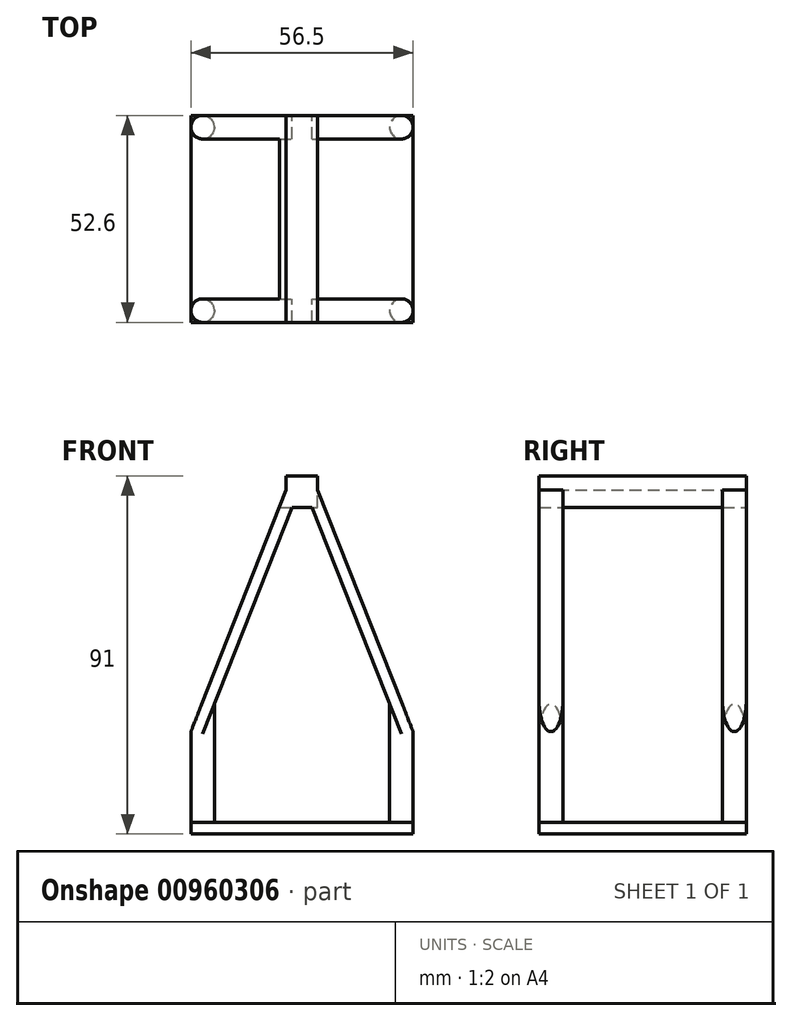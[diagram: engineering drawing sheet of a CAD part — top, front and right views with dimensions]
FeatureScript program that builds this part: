
annotation { "Feature Type Name" : "Feature", "Feature Type Description" : "" }
export const myFeature = defineFeature(function(context is Context, id is Id, definition is map)
    precondition{}
    {
        {
            var Q0;
            Q0=qCreatedBy(makeId("Front.planeOp"),FACE);
            var sketch = newSketch(context, id + "F0", { "sketchPlane" : qUnion([Q0])});
            skLineSegment(sketch, "E0", {"start": v(-28.25, 0) * mm, "end": v(-28.25, 22.98) * mm});
            skLineSegment(sketch, "E1.0", {"start": v(-22.25, 0) * mm, "end": v(-22.25, 30) * mm});
            skLineSegment(sketch, "E2", {"start": v(-25.25, 33.55) * mm, "end": v(-25.25, 26.27) * mm, "construction": true});
            skLineSegment(sketch, "E3", {"start": v(-28.25, 0) * mm, "end": v(-28.25, -3) * mm});
            skLineSegment(sketch, "E4", {"start": v(-28.25, 0) * mm, "end": v(-22.25, 0) * mm});
            skLineSegment(sketch, "E5", {"start": v(0, 87.78) * mm, "end": v(0, -3) * mm, "construction": true});
            skLineSegment(sketch, "E6", {"start": v(-2.5, 80) * mm, "end": v(0, 80) * mm});
            skLineSegment(sketch, "E7", {"start": v(-4, 84.37) * mm, "end": v(-4, 88) * mm});
            skLineSegment(sketch, "E8", {"start": v(-4, 88) * mm, "end": v(0, 88) * mm});
            skLineSegment(sketch, "E9", {"start": v(0, 88) * mm, "end": v(0, 87.78) * mm});
            skLineSegment(sketch, "E10", {"start": v(-22.25, 0) * mm, "end": v(0, 0) * mm});
            skLineSegment(sketch, "E11", {"start": v(0, -3) * mm, "end": v(-28.25, -3) * mm});
            skLineSegment(sketch, "E12", {"start": v(-48.17, 30) * mm, "end": v(25.31, 30) * mm, "construction": true});
            skLineSegment(sketch, "E13", {"start": v(-2.5, 80) * mm, "end": v(-22.25, 30) * mm});
            skLineSegment(sketch, "E14.0", {"start": v(-4, 84.37) * mm, "end": v(-28.25, 22.98) * mm});
            skPoint(sketch, "E15.orphan", {"position": v(-4, 80) * mm});
            skLineSegment(sketch, "E16", {"start": v(-22.25, 30) * mm, "end": v(-28.25, 22.98) * mm});
            skLineSegment(sketch, "E17", {"start": v(0, 80) * mm, "end": v(0, 87.78) * mm, "construction": true});
            skLineSegment(sketch, "E18", {"start": v(0, 87.78) * mm, "end": v(0, 80) * mm});
            skLineSegment(sketch, "E19", {"start": v(0, 0) * mm, "end": v(0, -3) * mm});
            skLineSegment(sketch, "E20.MirrorCS", {"start": v(4, 88) * mm, "end": v(0, 88) * mm});
            skLineSegment(sketch, "E21.MirrorCS", {"start": v(4, 84.37) * mm, "end": v(4, 88) * mm});
            skLineSegment(sketch, "E22.MirrorCS", {"start": v(4, 84.37) * mm, "end": v(28.25, 22.98) * mm});
            skLineSegment(sketch, "E23.MirrorCS", {"start": v(2.5, 80) * mm, "end": v(0, 80) * mm});
            skLineSegment(sketch, "E24.MirrorCS", {"start": v(2.5, 80) * mm, "end": v(22.25, 30) * mm});
            skLineSegment(sketch, "E25.MirrorCS", {"start": v(22.25, 30) * mm, "end": v(28.25, 22.98) * mm});
            skLineSegment(sketch, "E26.MirrorCS", {"start": v(22.25, 0) * mm, "end": v(22.25, 30) * mm});
            skLineSegment(sketch, "E27.MirrorCS", {"start": v(28.25, 0) * mm, "end": v(28.25, 22.98) * mm});
            skLineSegment(sketch, "E28.MirrorCS", {"start": v(28.25, 0) * mm, "end": v(22.25, 0) * mm});
            skLineSegment(sketch, "E29.MirrorCS", {"start": v(22.25, 0) * mm, "end": v(0, 0) * mm});
            skLineSegment(sketch, "E30.MirrorCS", {"start": v(0, -3) * mm, "end": v(28.25, -3) * mm});
            skLineSegment(sketch, "E31.MirrorCS", {"start": v(28.25, 0) * mm, "end": v(28.25, -3) * mm});
            skLineSegment(sketch, "E32", {"start": v(-28.25, 22.98) * mm, "end": v(-28.25, 30) * mm});
            skLineSegment(sketch, "E33", {"start": v(-28.25, 30) * mm, "end": v(-25.48, 30) * mm});
            skLineSegment(sketch, "E34", {"start": v(28.25, 22.98) * mm, "end": v(28.25, 30) * mm});
            skLineSegment(sketch, "E35", {"start": v(28.25, 30) * mm, "end": v(25.48, 30) * mm});
            skLineSegment(sketch, "E36", {"start": v(-22.25, 30) * mm, "end": v(-25.25, 22.4) * mm});
            skLineSegment(sketch, "E37", {"start": v(22.25, 30) * mm, "end": v(25.25, 22.4) * mm});
            skLineSegment(sketch, "E38", {"start": v(-25.25, 26.49) * mm, "end": v(-25.25, 22.4) * mm});
            skLineSegment(sketch, "E39", {"start": v(25.25, 22.4) * mm, "end": v(25.25, 26.49) * mm});
            skLineSegment(sketch, "E40", {"start": v(-4, 84.37) * mm, "end": v(-1.2, 83.27) * mm, "construction": true});
            skLineSegment(sketch, "E41", {"start": v(-2.5, 80) * mm, "end": v(-1.2, 83.27) * mm, "construction": true});
            skLineSegment(sketch, "E42", {"start": v(-28.25, 22.98) * mm, "end": v(-25.46, 21.87) * mm, "construction": true});
            skLineSegment(sketch, "E43", {"start": v(-25.25, 22.4) * mm, "end": v(-25.46, 21.87) * mm, "construction": true});
            skLineSegment(sketch, "E44", {"start": v(2.5, 80) * mm, "end": v(4, 80) * mm, "construction": true});
            skLineSegment(sketch, "E45", {"start": v(4, 80) * mm, "end": v(4, 84.37) * mm, "construction": true});
            skSolve(sketch);
        }
        {
            var Q0;
            Q0=makeQuery(id+"F0.imprint","IMPRINT",FACE,{"disambiguationData":[TD([[makeQuery(id+"F0.imprint","IMPRINT",EDGE,{"derivedFrom":sQuery(id+"F0.wireOp",EDGE,"E6")}),1.0]])]});
            var Q1;
            Q1=makeQuery(id+"F0.imprint","IMPRINT",FACE,{"disambiguationData":[TD([[makeQuery(id+"F0.imprint","IMPRINT",EDGE,{"derivedFrom":sQuery(id+"F0.wireOp",EDGE,"E9")}),1.0]])]});
            var Q2;
            Q2=makeQuery(id+"F0.imprint","IMPRINT",FACE,{"disambiguationData":[TD([[makeQuery(id+"F0.imprint","IMPRINT",EDGE,{"derivedFrom":sQuery(id+"F0.wireOp",EDGE,"E3")}),1.0]])]});
            var Q3;
            Q3=makeQuery(id+"F0.imprint","IMPRINT",FACE,{"disambiguationData":[TD([[makeQuery(id+"F0.imprint","IMPRINT",EDGE,{"derivedFrom":sQuery(id+"F0.wireOp",EDGE,"E19")}),1.0]])]});
            var Q4;
            {var subQ0=sQuery(id+"F0.wireOp",EDGE,"E36");Q4=makeQuery(id+"F0.imprint","IMPRINT",FACE,{"disambiguationData":[TD([[makeQuery(id+"F0.imprint","IMPRINT",EDGE,{"derivedFrom":subQ0}),-1.0]])]});}
            var Q5;
            {var subQ0=sQuery(id+"F0.wireOp",EDGE,"E37");Q5=makeQuery(id+"F0.imprint","IMPRINT",FACE,{"disambiguationData":[TD([[makeQuery(id+"F0.imprint","IMPRINT",EDGE,{"derivedFrom":subQ0}),1.0]])]});}
            extrude(context, id + "F1", {"entities" : qUnion([Q0, Q1, Q2, Q3, Q4, Q5]), "endBound" : BoundingType.SYMMETRIC, "depth" : 52.6 * mm, "offsetDistance" : 25 * mm});
        }
        {
            var Q0;
            Q0=qCreatedBy(makeId("Top.planeOp"),FACE);
            var sketch = newSketch(context, id + "F2", { "sketchPlane" : qUnion([Q0])});
            skLineSegment(sketch, "E46.0.0", {"start": v(28.25, 26.3) * mm, "end": v(-28.25, 26.3) * mm});
            skLineSegment(sketch, "E46.0.1", {"start": v(-28.25, 26.3) * mm, "end": v(-28.25, -26.3) * mm});
            skLineSegment(sketch, "E46.0.2", {"start": v(-28.25, -26.3) * mm, "end": v(28.25, -26.3) * mm});
            skLineSegment(sketch, "E46.0.3", {"start": v(28.25, -26.3) * mm, "end": v(28.25, 26.3) * mm});
            skCircle(sketch, "E47", {"center": v(-25.25, 23.3) * mm, "radius": 3 * mm});
            skCircle(sketch, "E48", {"center": v(25.25, 23.3) * mm, "radius": 3 * mm});
            skCircle(sketch, "E49", {"center": v(-25.25, -23.3) * mm, "radius": 3 * mm});
            skCircle(sketch, "E50", {"center": v(25.25, -23.3) * mm, "radius": 3 * mm});
            skSolve(sketch);
        }
        {
            var Q0;
            {var subQ0=sQuery(id+"F2.wireOp",EDGE,"E47");var subQ1=makeQuery(id+"F2.imprint","INTERSECT",VERTEX,{"derivedFrom":[sQuery(id+"F2.wireOp",EDGE,"E46.0.0"),subQ0]});Q0=makeQuery(id+"F2.imprint","IMPRINT",FACE,{"disambiguationData":[TD([[makeQuery(id+"F2.imprint","IMPRINT",EDGE,{"disambiguationData":[TD([[subQ1,-1.0]])],"derivedFrom":subQ0}),1.0]])]});}
            var Q1;
            {var subQ0=sQuery(id+"F2.wireOp",EDGE,"E49");var subQ1=makeQuery(id+"F2.imprint","INTERSECT",VERTEX,{"derivedFrom":[sQuery(id+"F2.wireOp",EDGE,"E46.0.1"),subQ0]});Q1=makeQuery(id+"F2.imprint","IMPRINT",FACE,{"disambiguationData":[TD([[makeQuery(id+"F2.imprint","IMPRINT",EDGE,{"disambiguationData":[TD([[subQ1,-1.0]])],"derivedFrom":subQ0}),1.0]])]});}
            var Q2;
            {var subQ0=sQuery(id+"F2.wireOp",EDGE,"E48");var subQ1=makeQuery(id+"F2.imprint","INTERSECT",VERTEX,{"derivedFrom":[sQuery(id+"F2.wireOp",EDGE,"E46.0.0"),subQ0]});Q2=makeQuery(id+"F2.imprint","IMPRINT",FACE,{"disambiguationData":[TD([[makeQuery(id+"F2.imprint","IMPRINT",EDGE,{"disambiguationData":[TD([[subQ1,1.0]])],"derivedFrom":subQ0}),1.0]])]});}
            var Q3;
            {var subQ0=sQuery(id+"F2.wireOp",EDGE,"E50");var subQ1=makeQuery(id+"F2.imprint","INTERSECT",VERTEX,{"derivedFrom":[sQuery(id+"F2.wireOp",EDGE,"E46.0.2"),subQ0]});Q3=makeQuery(id+"F2.imprint","IMPRINT",FACE,{"disambiguationData":[TD([[makeQuery(id+"F2.imprint","IMPRINT",EDGE,{"disambiguationData":[TD([[subQ1,1.0]])],"derivedFrom":subQ0}),1.0]])]});}
            extrude(context, id + "F3", {"entities" : qUnion([Q0, Q1, Q2, Q3]), "depth" : 30 * mm, "offsetDistance" : 25 * mm});
        }
        {
            var Q0;
            Q0=makeQuery(id+"F3.opExtrude","CAP_FACE",FACE,{"disambiguationData":[OSD([sQuery(id+"F2.wireOp",EDGE,"E48")])],"isStart":false});
            cPlane(context, id + "F4", {"entities" : qUnion([Q0]), "cplaneType" : CPlaneType.OFFSET, "offset" : 0 * mm, "width" : 150 * mm, "height" : 150 * mm});
        }
        {
            var Q0;
            Q0=qCreatedBy(id+"F4.planeOp",FACE);
            var sketch = newSketch(context, id + "F5", { "sketchPlane" : qUnion([Q0])});
            skLineSegment(sketch, "E51.0", {"start": v(28.25, -26.3) * mm, "end": v(28.25, -23.3) * mm});
            skLineSegment(sketch, "E52.0", {"start": v(25.25, 26.3) * mm, "end": v(28.25, 26.3) * mm});
            skLineSegment(sketch, "E53.0", {"start": v(-25.25, 26.3) * mm, "end": v(-28.25, 26.3) * mm});
            skLineSegment(sketch, "E54.0", {"start": v(-28.25, -26.3) * mm, "end": v(-28.25, -23.3) * mm});
            skLineSegment(sketch, "E55.0", {"start": v(-25.25, -26.3) * mm, "end": v(-28.25, -26.3) * mm});
            skLineSegment(sketch, "E56.0", {"start": v(25.25, -26.3) * mm, "end": v(28.25, -26.3) * mm});
            skArc(sketch, "E57.0", {"start": v(28.25, 23.3) * mm, "mid": v(27.37, 25.42) * mm, "end": v(25.25, 26.3) * mm});
            skArc(sketch, "E58.0", {"start": v(25.25, -26.3) * mm, "mid": v(27.37, -25.42) * mm, "end": v(28.25, -23.3) * mm});
            skArc(sketch, "E59.0", {"start": v(-28.25, -23.3) * mm, "mid": v(-27.37, -25.42) * mm, "end": v(-25.25, -26.3) * mm});
            skArc(sketch, "E60.0", {"start": v(-25.25, 26.3) * mm, "mid": v(-27.37, 25.42) * mm, "end": v(-28.25, 23.3) * mm});
            skLineSegment(sketch, "E61.trimOffspring", {"start": v(-28.25, 23.3) * mm, "end": v(-28.25, 26.3) * mm});
            skPoint(sketch, "E62.orphan", {"position": v(-4, 26.3) * mm});
            skPoint(sketch, "E63.orphan", {"position": v(-4, -26.3) * mm});
            skPoint(sketch, "E64.orphan", {"position": v(4, 26.3) * mm});
            skLineSegment(sketch, "E65.trimOffspring", {"start": v(28.25, 23.3) * mm, "end": v(28.25, 26.3) * mm});
            skPoint(sketch, "E66.orphan", {"position": v(4, -26.3) * mm});
            skLineSegment(sketch, "E67.0", {"start": v(-28.25, -26.3) * mm, "end": v(-28.25, -20.3) * mm});
            skLineSegment(sketch, "E68.0", {"start": v(28.25, -26.3) * mm, "end": v(28.25, -20.3) * mm});
            skCircle(sketch, "E69.0", {"center": v(25.25, 23.3) * mm, "radius": 3 * mm});
            skCircle(sketch, "E70.0.0", {"center": v(25.25, -23.3) * mm, "radius": 3 * mm});
            skCircle(sketch, "E71.0.0", {"center": v(-25.25, -23.3) * mm, "radius": 3 * mm});
            skCircle(sketch, "E72.0.0", {"center": v(-25.25, 23.3) * mm, "radius": 3 * mm});
            skLineSegment(sketch, "E73", {"start": v(-25.25, 20.3) * mm, "end": v(-28.25, 20.3) * mm});
            skLineSegment(sketch, "E74", {"start": v(25.25, 20.3) * mm, "end": v(28.25, 20.3) * mm});
            skLineSegment(sketch, "E75", {"start": v(25.25, -20.3) * mm, "end": v(28.25, -20.3) * mm});
            skLineSegment(sketch, "E76", {"start": v(-25.25, -20.3) * mm, "end": v(-28.25, -20.3) * mm});
            skLineSegment(sketch, "E77.trimOffspring", {"start": v(-28.25, 20.3) * mm, "end": v(-28.25, 26.3) * mm});
            skLineSegment(sketch, "E78.trimOffspring", {"start": v(28.25, 20.3) * mm, "end": v(28.25, 26.3) * mm});
            skSolve(sketch);
        }
        {
            var Q0;
            Q0=makeQuery(id+"F1.opExtrude","SWEPT_BODY",BODY,{"disambiguationData":[OSD([sQuery(id+"F0.wireOp",EDGE,"E3"),sQuery(id+"F0.wireOp",EDGE,"E4"),sQuery(id+"F0.wireOp",EDGE,"E10"),sQuery(id+"F0.wireOp",EDGE,"E11"),sQuery(id+"F0.wireOp",EDGE,"E28.MirrorCS"),sQuery(id+"F0.wireOp",EDGE,"E29.MirrorCS"),sQuery(id+"F0.wireOp",EDGE,"E30.MirrorCS"),sQuery(id+"F0.wireOp",EDGE,"E31.MirrorCS")])]});
            var Q1;
            Q1=makeQuery(id+"F3.opExtrude","SWEPT_BODY",BODY,{"disambiguationData":[OSD([sQuery(id+"F2.wireOp",EDGE,"E49")])]});
            var Q2;
            Q2=makeQuery(id+"F3.opExtrude","SWEPT_BODY",BODY,{"disambiguationData":[OSD([sQuery(id+"F2.wireOp",EDGE,"E47")])]});
            var Q3;
            Q3=makeQuery(id+"F3.opExtrude","SWEPT_BODY",BODY,{"disambiguationData":[OSD([sQuery(id+"F2.wireOp",EDGE,"E48")])]});
            var Q4;
            Q4=makeQuery(id+"F3.opExtrude","SWEPT_BODY",BODY,{"disambiguationData":[OSD([sQuery(id+"F2.wireOp",EDGE,"E50")])]});
            var Q5;
            Q5=makeQuery(id+"F1.opExtrude","SWEPT_BODY",BODY,{"disambiguationData":[OSD([sQuery(id+"F0.wireOp",EDGE,"E6"),sQuery(id+"F0.wireOp",EDGE,"E7"),sQuery(id+"F0.wireOp",EDGE,"E8"),sQuery(id+"F0.wireOp",EDGE,"E13"),sQuery(id+"F0.wireOp",EDGE,"E14.0"),sQuery(id+"F0.wireOp",EDGE,"E16"),sQuery(id+"F0.wireOp",EDGE,"E20.MirrorCS"),sQuery(id+"F0.wireOp",EDGE,"E21.MirrorCS"),sQuery(id+"F0.wireOp",EDGE,"E22.MirrorCS"),sQuery(id+"F0.wireOp",EDGE,"E23.MirrorCS"),sQuery(id+"F0.wireOp",EDGE,"E24.MirrorCS"),sQuery(id+"F0.wireOp",EDGE,"E25.MirrorCS")])]});
            booleanBodies(context, id + "F6", {"operationType" : BooleanOperationType.UNION, "tools" : qUnion([Q0, Q1, Q2, Q3, Q4, Q5])});
        }
        {
            var Q0;
            {var subQ0=sQuery(id+"F5.wireOp",EDGE,"E53.0");Q0=makeQuery(id+"F5.imprint","IMPRINT",FACE,{"disambiguationData":[TD([[makeQuery(id+"F5.imprint","IMPRINT",EDGE,{"derivedFrom":subQ0}),1.0]])]});}
            var Q1;
            {var subQ0=sQuery(id+"F5.wireOp",EDGE,"E73");Q1=makeQuery(id+"F5.imprint","IMPRINT",FACE,{"disambiguationData":[TD([[makeQuery(id+"F5.imprint","IMPRINT",EDGE,{"derivedFrom":subQ0}),-1.0]])]});}
            var Q2;
            {var subQ0=sQuery(id+"F5.wireOp",EDGE,"E52.0");Q2=makeQuery(id+"F5.imprint","IMPRINT",FACE,{"disambiguationData":[TD([[makeQuery(id+"F5.imprint","IMPRINT",EDGE,{"derivedFrom":subQ0}),-1.0]])]});}
            var Q3;
            {var subQ0=sQuery(id+"F5.wireOp",EDGE,"E74");Q3=makeQuery(id+"F5.imprint","IMPRINT",FACE,{"disambiguationData":[TD([[makeQuery(id+"F5.imprint","IMPRINT",EDGE,{"derivedFrom":subQ0}),1.0]])]});}
            var Q4;
            {var subQ0=sQuery(id+"F5.wireOp",EDGE,"E75");Q4=makeQuery(id+"F5.imprint","IMPRINT",FACE,{"disambiguationData":[TD([[makeQuery(id+"F5.imprint","IMPRINT",EDGE,{"derivedFrom":subQ0}),-1.0]])]});}
            var Q5;
            {var subQ0=sQuery(id+"F5.wireOp",EDGE,"E56.0");Q5=makeQuery(id+"F5.imprint","IMPRINT",FACE,{"disambiguationData":[TD([[makeQuery(id+"F5.imprint","IMPRINT",EDGE,{"derivedFrom":subQ0}),1.0]])]});}
            var Q6;
            {var subQ0=sQuery(id+"F5.wireOp",EDGE,"E76");Q6=makeQuery(id+"F5.imprint","IMPRINT",FACE,{"disambiguationData":[TD([[makeQuery(id+"F5.imprint","IMPRINT",EDGE,{"derivedFrom":subQ0}),1.0]])]});}
            var Q7;
            {var subQ0=sQuery(id+"F5.wireOp",EDGE,"E55.0");Q7=makeQuery(id+"F5.imprint","IMPRINT",FACE,{"disambiguationData":[TD([[makeQuery(id+"F5.imprint","IMPRINT",EDGE,{"derivedFrom":subQ0}),-1.0]])]});}
            extrude(context, id + "F7", {"entities" : qUnion([Q0, Q1, Q2, Q3, Q4, Q5, Q6, Q7]), "operationType" : NewBodyOperationType.REMOVE, "oppositeDirection" : true, "depth" : 8 * mm, "offsetDistance" : 25 * mm});
        }
        {
            var Q0;
            {var subQ0=sQuery(id+"F0.wireOp",EDGE,"E34");Q0=makeQuery(id+"F0.imprint","IMPRINT",FACE,{"disambiguationData":[TD([[makeQuery(id+"F0.imprint","IMPRINT",EDGE,{"derivedFrom":subQ0}),1.0]])]});}
            var Q1;
            {var subQ0=sQuery(id+"F0.wireOp",EDGE,"E32");Q1=makeQuery(id+"F0.imprint","IMPRINT",FACE,{"disambiguationData":[TD([[makeQuery(id+"F0.imprint","IMPRINT",EDGE,{"derivedFrom":subQ0}),-1.0]])]});}
            extrude(context, id + "F8", {"entities" : qUnion([Q0, Q1]), "operationType" : NewBodyOperationType.REMOVE, "endBound" : BoundingType.SYMMETRIC, "oppositeDirection" : true, "depth" : 60 * mm, "offsetDistance" : 25 * mm});
        }
        {
            var Q0;
            Q0=qCreatedBy(makeId("Right.planeOp"),FACE);
            var sketch = newSketch(context, id + "F9", { "sketchPlane" : qUnion([Q0])});
            skLineSegment(sketch, "E79.0", {"start": v(-23.3, 0) * mm, "end": v(23.3, 0) * mm});
            skLineSegment(sketch, "E80", {"start": v(20.3, 0) * mm, "end": v(20.3, 80) * mm});
            skLineSegment(sketch, "E81", {"start": v(-20.3, 0) * mm, "end": v(-20.3, 80) * mm});
            skLineSegment(sketch, "E82", {"start": v(20.3, 80) * mm, "end": v(-20.3, 80) * mm});
            skSolve(sketch);
        }
        {
            var Q0;
            {var subQ0=sQuery(id+"F9.wireOp",EDGE,"E80");Q0=makeQuery(id+"F9.imprint","IMPRINT",FACE,{"disambiguationData":[TD([[makeQuery(id+"F9.imprint","IMPRINT",EDGE,{"derivedFrom":subQ0}),1.0]])]});}
            extrude(context, id + "F10", {"entities" : qUnion([Q0]), "operationType" : NewBodyOperationType.REMOVE, "endBound" : BoundingType.SYMMETRIC, "oppositeDirection" : true, "depth" : 60 * mm, "offsetDistance" : 25 * mm});
        }
        {
            var Q0;
            Q0=makeQuery(id+"F1.opExtrude","SWEPT_FACE",FACE,{"disambiguationData":[OSD([sQuery(id+"F0.wireOp",EDGE,"E8"),sQuery(id+"F0.wireOp",EDGE,"E20.MirrorCS")])]});
            cPlane(context, id + "F11", {"entities" : qUnion([Q0]), "cplaneType" : CPlaneType.OFFSET, "offset" : 0 * mm, "width" : 150 * mm, "height" : 150 * mm});
        }
        {
            var Q0;
            Q0=qCreatedBy(id+"F11.planeOp",FACE);
            var sketch = newSketch(context, id + "F12", { "sketchPlane" : qUnion([Q0])});
            skLineSegment(sketch, "E83.0.1", {"start": v(-4, 20.3) * mm, "end": v(-4, -20.3) * mm});
            skLineSegment(sketch, "E83.0.3", {"start": v(4, -20.3) * mm, "end": v(4, 20.3) * mm});
            skLineSegment(sketch, "E84.0.2", {"start": v(5.73, -20.3) * mm, "end": v(5.73, 20.3) * mm});
            skLineSegment(sketch, "E84.0.8", {"start": v(4, 20.3) * mm, "end": v(4, -20.3) * mm});
            skLineSegment(sketch, "E85.0.5", {"start": v(-4, -20.3) * mm, "end": v(-4, 20.3) * mm});
            skLineSegment(sketch, "E85.0.11", {"start": v(-5.73, 20.3) * mm, "end": v(-5.73, -20.3) * mm});
            skLineSegment(sketch, "E86", {"start": v(-5.73, 20.3) * mm, "end": v(-4, 20.3) * mm});
            skLineSegment(sketch, "E87", {"start": v(5.73, -20.3) * mm, "end": v(4, -20.3) * mm});
            skLineSegment(sketch, "E88.trimOffspring", {"start": v(4, 20.3) * mm, "end": v(5.73, 20.3) * mm});
            skLineSegment(sketch, "E89.trimOffspring", {"start": v(-4, -20.3) * mm, "end": v(-5.73, -20.3) * mm});
            skSolve(sketch);
        }
        {
            var Q0;
            Q0=makeQuery(id+"F12.imprint","IMPRINT",FACE,{"disambiguationData":[TD([[makeQuery(id+"F12.imprint","IMPRINT",EDGE,{"derivedFrom":sQuery(id+"F12.wireOp",EDGE,"E85.0.5")}),1.0]])]});
            var Q1;
            Q1=makeQuery(id+"F12.imprint","IMPRINT",FACE,{"disambiguationData":[TD([[makeQuery(id+"F12.imprint","IMPRINT",EDGE,{"derivedFrom":sQuery(id+"F12.wireOp",EDGE,"E84.0.2")}),1.0]])]});
            extrude(context, id + "F13", {"entities" : qUnion([Q0, Q1]), "operationType" : NewBodyOperationType.REMOVE, "oppositeDirection" : true, "depth" : 25 * mm, "offsetDistance" : 25 * mm});
        }
    });
